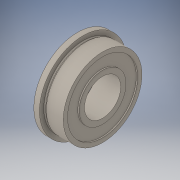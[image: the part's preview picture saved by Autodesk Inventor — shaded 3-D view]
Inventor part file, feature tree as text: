
AUTODESK INVENTOR PART (.ipt)
format: ipt  version: 2018 (Build 220112000, 112)  size: 174,592 bytes
history: native  units: in
note: dims shown in document units (in); Inventor stores cm internally (conversion verified against a paired STEP export)
features: revolve x1
ambient origin geometry x8: Origin, YZ Plane, XZ Plane, XY Plane, X Axis, Y Axis, Z Axis, Center Point
bodies: Solid1 (feature_tree)
feature tree (1):
  revolve  "Revolve1"  [1 undecoded]
note: 1 required parameter value undecoded (feature->parameter linkage not recoverable at this tier; creation-order binding heuristic only, values carry confidence <= 0.55)
